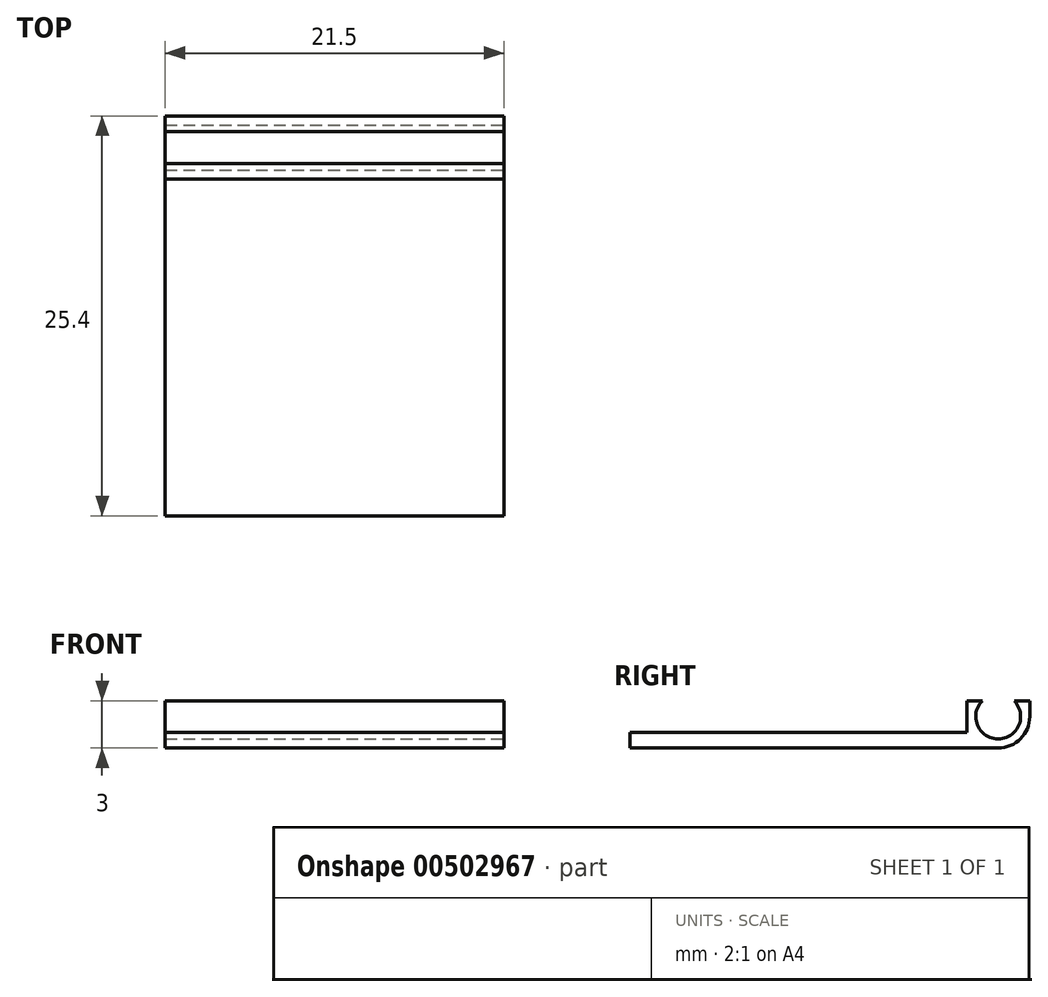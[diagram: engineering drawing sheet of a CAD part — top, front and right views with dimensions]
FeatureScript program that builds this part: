
annotation { "Feature Type Name" : "Feature", "Feature Type Description" : "" }
export const myFeature = defineFeature(function(context is Context, id is Id, definition is map)
    precondition{}
    {
        {
            var Q0;
            Q0=qCreatedBy(makeId("Top.planeOp"),FACE);
            var sketch = newSketch(context, id + "F0", { "sketchPlane" : qUnion([Q0])});
            skLineSegment(sketch, "E0.bottom", {"start": v(10.75, 10.7) * mm, "end": v(-10.75, 10.7) * mm});
            skLineSegment(sketch, "E0.top", {"start": v(10.75, -10.7) * mm, "end": v(-10.75, -10.7) * mm});
            skLineSegment(sketch, "E0.left", {"start": v(10.75, 10.7) * mm, "end": v(10.75, -10.7) * mm});
            skLineSegment(sketch, "E0.right", {"start": v(-10.75, 10.7) * mm, "end": v(-10.75, -10.7) * mm});
            skPoint(sketch, "E0.middle", {"position": v(0, 0) * mm});
            skLineSegment(sketch, "E1.top", {"start": v(10.75, 14.7) * mm, "end": v(-10.75, 14.7) * mm});
            skLineSegment(sketch, "E1.left", {"start": v(10.75, 10.7) * mm, "end": v(10.75, 14.7) * mm});
            skLineSegment(sketch, "E1.right", {"start": v(-10.75, 10.7) * mm, "end": v(-10.75, 14.7) * mm});
            skLineSegment(sketch, "E2.bottom", {"start": v(-10.75, -10.7) * mm, "end": v(10.75, -10.7) * mm});
            skLineSegment(sketch, "E2.top", {"start": v(-10.75, -14.7) * mm, "end": v(10.75, -14.7) * mm});
            skLineSegment(sketch, "E2.left", {"start": v(-10.75, -10.7) * mm, "end": v(-10.75, -14.7) * mm});
            skLineSegment(sketch, "E2.right", {"start": v(10.75, -10.7) * mm, "end": v(10.75, -14.7) * mm});
            skSolve(sketch);
        }
        {
            var Q0;
            Q0=makeQuery(id+"F0.imprint","IMPRINT",FACE,{"disambiguationData":[TD([[makeQuery(id+"F0.imprint","IMPRINT",EDGE,{"derivedFrom":sQuery(id+"F0.wireOp",EDGE,"E0.left")}),-1.0]])]});
            extrude(context, id + "F1", {"entities" : qUnion([Q0]), "depth" : 1 * mm});
        }
        {
            var Q0;
            Q0=makeQuery(id+"F0.imprint","IMPRINT",FACE,{"disambiguationData":[TD([[makeQuery(id+"F0.imprint","IMPRINT",EDGE,{"derivedFrom":sQuery(id+"F0.wireOp",EDGE,"E0.bottom")}),-1.0]])]});
            var Q1;
            Q1=makeQuery(id+"F0.imprint","IMPRINT",FACE,{"disambiguationData":[TD([[makeQuery(id+"F0.imprint","IMPRINT",EDGE,{"derivedFrom":sQuery(id+"F0.wireOp",EDGE,"E2.bottom")}),-1.0]])]});
            extrude(context, id + "F2", {"entities" : qUnion([Q0, Q1]), "operationType" : NewBodyOperationType.ADD, "depth" : 3 * mm});
        }
        {
            var Q0;
            Q0=makeQuery(id+"F2.boolean.opBoolean","MERGE",FACE,{"derivedFrom":[makeQuery(id+"F1.opExtrude","SWEPT_FACE",FACE,{"disambiguationData":[OSD([sQuery(id+"F0.wireOp",EDGE,"E0.left")])]}),makeQuery(id+"F2.opExtrude","SWEPT_FACE",FACE,{"disambiguationData":[OSD([sQuery(id+"F0.wireOp",EDGE,"E1.left")])]}),makeQuery(id+"F2.opExtrude","SWEPT_FACE",FACE,{"disambiguationData":[OSD([sQuery(id+"F0.wireOp",EDGE,"E2.right")])]})]});
            var sketch = newSketch(context, id + "F3", { "sketchPlane" : qUnion([Q0])});
            skPoint(sketch, "E3", {"position": v(12.7, 2) * mm});
            skPoint(sketch, "E3.positionSnap0", {"position": v(12.7, 3) * mm});
            skPoint(sketch, "E4", {"position": v(-12.7, 2) * mm});
            skPoint(sketch, "E4.positionSnap0", {"position": v(-12.7, 3) * mm});
            skSolve(sketch);
        }
        {
            var Q0;
            Q0=sQuery(id+"F3.wireOp",VERTEX,"E3");
            var Q1;
            Q1=sQuery(id+"F3.wireOp",VERTEX,"E4");
            var Q2;
            Q2=makeQuery(id+"F1.opExtrude","SWEPT_BODY",BODY,{"disambiguationData":[OSD([sQuery(id+"F0.wireOp",EDGE,"E0.left"),sQuery(id+"F0.wireOp",EDGE,"E0.right"),sQuery(id+"F0.wireOp",EDGE,"E0.bottom"),sQuery(id+"F0.wireOp",EDGE,"E2.bottom")])]});
            hole(context, id + "F4", {"style" : HoleStyle.SIMPLE, "endStyle" : HoleEndStyle.THROUGH, "holeDiameter" : 2.85 * mm, "isTappedThrough" : true, "tappedDepth" : 12 * mm, "tapClearance" : 3, "locations" : qUnion([Q0, Q1]), "scope" : qUnion([Q2])});
        }
        {
            var Q0;
            Q0=makeQuery(id+"F2.opExtrude","CAP_EDGE",EDGE,{"disambiguationData":[OSD([sQuery(id+"F0.wireOp",EDGE,"E1.top")])],"isStart":true});
            var Q1;
            Q1=makeQuery(id+"F2.opExtrude","CAP_EDGE",EDGE,{"disambiguationData":[OSD([sQuery(id+"F0.wireOp",EDGE,"E2.top")])],"isStart":true});
            fillet(context, id + "F5", {"entities" : qUnion([Q0, Q1]), "radius" : 2 * mm, "tangentPropagation" : true, "allowEdgeOverflow" : false});
        }
    });
